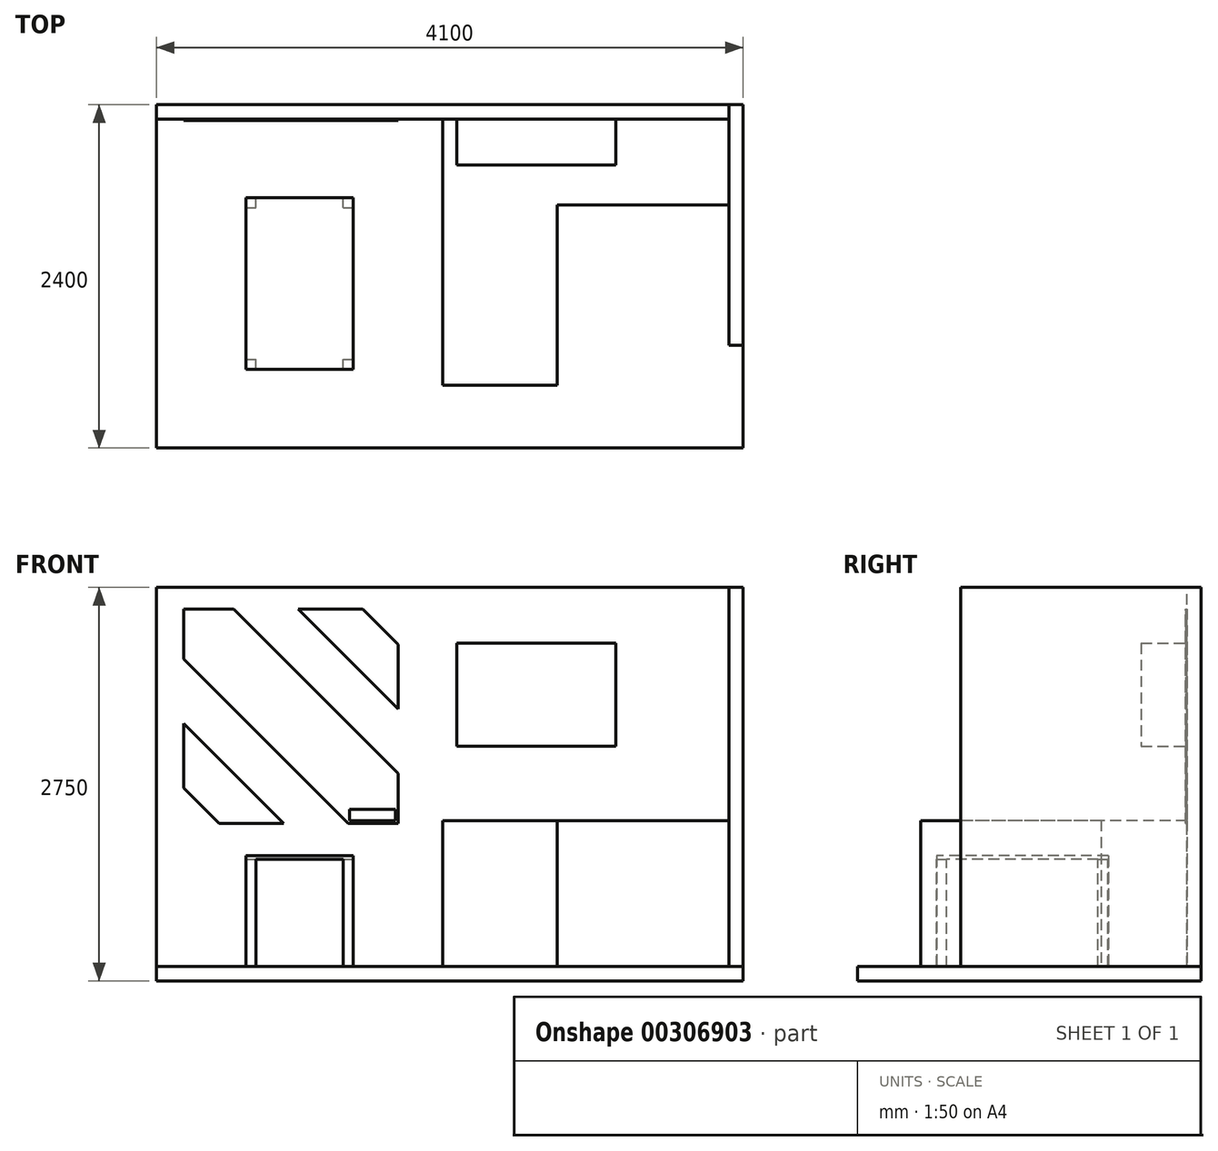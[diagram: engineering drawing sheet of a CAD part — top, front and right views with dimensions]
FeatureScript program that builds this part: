
annotation { "Feature Type Name" : "Feature", "Feature Type Description" : "" }
export const myFeature = defineFeature(function(context is Context, id is Id, definition is map)
    precondition{}
    {
        {
            var Q0;
            Q0=qCreatedBy(makeId("Top.planeOp"),FACE);
            var sketch = newSketch(context, id + "F0", { "sketchPlane" : qUnion([Q0])});
            skLineSegment(sketch, "E0.bottom", {"start": v(0, 0) * mm, "end": v(800, 0) * mm});
            skLineSegment(sketch, "E0.top", {"start": v(0, -1860) * mm, "end": v(800, -1860) * mm});
            skLineSegment(sketch, "E0.left", {"start": v(0, 0) * mm, "end": v(0, -1860) * mm});
            skLineSegment(sketch, "E0.right", {"start": v(800, -600) * mm, "end": v(800, -1860) * mm});
            skLineSegment(sketch, "E1", {"start": v(800, 0) * mm, "end": v(2000, 0) * mm});
            skLineSegment(sketch, "E2", {"start": v(2000, 0) * mm, "end": v(2000, -600) * mm});
            skLineSegment(sketch, "E3", {"start": v(2000, -600) * mm, "end": v(800, -600) * mm});
            skSolve(sketch);
        }
        {
            var Q0;
            Q0=makeQuery(id+"F0.imprint","IMPRINT",FACE,{"disambiguationData":[TD([[makeQuery(id+"F0.imprint","IMPRINT",EDGE,{"derivedFrom":sQuery(id+"F0.wireOp",EDGE,"E0.bottom")}),-1.0]])]});
            extrude(context, id + "F1", {"entities" : qUnion([Q0]), "depth" : 1020 * mm});
        }
        {
            var Q0;
            Q0=makeQuery(id+"F1.opExtrude","SWEPT_FACE",FACE,{"disambiguationData":[OSD([sQuery(id+"F0.wireOp",EDGE,"E0.bottom"),sQuery(id+"F0.wireOp",EDGE,"E1")])]});
            cPlane(context, id + "F2", {"entities" : qUnion([Q0]), "cplaneType" : CPlaneType.OFFSET, "offset" : 0 * mm, "width" : 150 * mm, "height" : 150 * mm});
        }
        {
            var Q0;
            Q0=qCreatedBy(id+"F2.planeOp",FACE);
            var sketch = newSketch(context, id + "F3", { "sketchPlane" : qUnion([Q0])});
            skLineSegment(sketch, "E4.0", {"start": v(0, 1020) * mm, "end": v(0, 0) * mm, "construction": true});
            skLineSegment(sketch, "E5.bottom", {"start": v(0, 0) * mm, "end": v(2000, 0) * mm});
            skLineSegment(sketch, "E5.top", {"start": v(0, 2650) * mm, "end": v(2000, 2650) * mm});
            skLineSegment(sketch, "E5.left", {"start": v(0, 0) * mm, "end": v(0, 2650) * mm, "construction": true});
            skLineSegment(sketch, "E5.right", {"start": v(2000, 0) * mm, "end": v(2000, 2650) * mm});
            skLineSegment(sketch, "E6.0", {"start": v(-2000, 1020) * mm, "end": v(-2000, 0) * mm, "construction": true});
            skLineSegment(sketch, "E7.bottom", {"start": v(0, 0) * mm, "end": v(-2000, 0) * mm});
            skLineSegment(sketch, "E7.top", {"start": v(0, 2650) * mm, "end": v(-2000, 2650) * mm});
            skLineSegment(sketch, "E7.right", {"start": v(-2000, 0) * mm, "end": v(-2000, 2650) * mm});
            skLineSegment(sketch, "E8.bottom", {"start": v(-1210, 2260) * mm, "end": v(-100, 2260) * mm});
            skLineSegment(sketch, "E8.top", {"start": v(-1210, 1540) * mm, "end": v(-100, 1540) * mm});
            skLineSegment(sketch, "E8.left", {"start": v(-1210, 2260) * mm, "end": v(-1210, 1540) * mm});
            skLineSegment(sketch, "E8.right", {"start": v(-100, 2260) * mm, "end": v(-100, 1540) * mm});
            skSolve(sketch);
        }
        {
            var Q0;
            Q0=makeQuery(id+"F3.imprint","IMPRINT",FACE,{"disambiguationData":[TD([[makeQuery(id+"F3.imprint","IMPRINT",EDGE,{"derivedFrom":sQuery(id+"F3.wireOp",EDGE,"E5.bottom")}),1.0]])]});
            var Q1;
            Q1=makeQuery(id+"F3.imprint","IMPRINT",FACE,{"disambiguationData":[TD([[makeQuery(id+"F3.imprint","IMPRINT",EDGE,{"derivedFrom":sQuery(id+"F3.wireOp",EDGE,"E8.bottom")}),-1.0]])]});
            extrude(context, id + "F4", {"entities" : qUnion([Q0, Q1]), "depth" : 100 * mm});
        }
        {
            var Q0;
            Q0=makeQuery(id+"F3.imprint","IMPRINT",FACE,{"disambiguationData":[TD([[makeQuery(id+"F3.imprint","IMPRINT",EDGE,{"derivedFrom":sQuery(id+"F3.wireOp",EDGE,"E8.bottom")}),-1.0]])]});
            extrude(context, id + "F5", {"entities" : qUnion([Q0]), "oppositeDirection" : true, "depth" : 320 * mm});
        }
        {
            var Q0;
            Q0=makeQuery(id+"F1.opExtrude","SWEPT_FACE",FACE,{"disambiguationData":[OSD([sQuery(id+"F0.wireOp",EDGE,"E2")])]});
            cPlane(context, id + "F6", {"entities" : qUnion([Q0]), "cplaneType" : CPlaneType.OFFSET, "offset" : 0 * mm, "width" : 150 * mm, "height" : 150 * mm});
        }
        {
            var Q0;
            Q0=qCreatedBy(id+"F6.planeOp",FACE);
            var sketch = newSketch(context, id + "F7", { "sketchPlane" : qUnion([Q0])});
            skPoint(sketch, "E9.0", {"position": v(100, 0) * mm});
            skPoint(sketch, "E10.0", {"position": v(100, 2650) * mm});
            skLineSegment(sketch, "E11.bottom", {"start": v(100, 0) * mm, "end": v(-1580, 0) * mm});
            skLineSegment(sketch, "E11.top", {"start": v(100, 2650) * mm, "end": v(-1580, 2650) * mm});
            skLineSegment(sketch, "E11.left", {"start": v(100, 0) * mm, "end": v(100, 2650) * mm});
            skLineSegment(sketch, "E11.right", {"start": v(-1580, 0) * mm, "end": v(-1580, 2650) * mm});
            skSolve(sketch);
        }
        {
            var Q0;
            Q0=makeQuery(id+"F7.imprint","IMPRINT",FACE,{"disambiguationData":[TD([[makeQuery(id+"F7.imprint","IMPRINT",EDGE,{"derivedFrom":sQuery(id+"F7.wireOp",EDGE,"E11.bottom")}),-1.0]])]});
            extrude(context, id + "F8", {"entities" : qUnion([Q0]), "depth" : 100 * mm});
        }
        {
            var Q0;
            Q0=makeQuery(id+"F1.opExtrude","CAP_FACE",FACE,{"disambiguationData":[OSD([sQuery(id+"F0.wireOp",EDGE,"E0.bottom"),sQuery(id+"F0.wireOp",EDGE,"E0.top"),sQuery(id+"F0.wireOp",EDGE,"E0.left"),sQuery(id+"F0.wireOp",EDGE,"E0.right"),sQuery(id+"F0.wireOp",EDGE,"E1"),sQuery(id+"F0.wireOp",EDGE,"E2"),sQuery(id+"F0.wireOp",EDGE,"E3")])],"isStart":true});
            cPlane(context, id + "F9", {"entities" : qUnion([Q0]), "cplaneType" : CPlaneType.OFFSET, "offset" : 0 * mm, "width" : 150 * mm, "height" : 150 * mm});
        }
        {
            var Q0;
            Q0=qCreatedBy(id+"F9.planeOp",FACE);
            var sketch = newSketch(context, id + "F10", { "sketchPlane" : qUnion([Q0])});
            skPoint(sketch, "E12.0", {"position": v(2100, -100) * mm});
            skPoint(sketch, "E13.0", {"position": v(-2000, -100) * mm});
            skLineSegment(sketch, "E14.bottom", {"start": v(2100, -100) * mm, "end": v(-2000, -100) * mm});
            skLineSegment(sketch, "E14.top", {"start": v(2100, 2300) * mm, "end": v(-2000, 2300) * mm});
            skLineSegment(sketch, "E14.left", {"start": v(2100, -100) * mm, "end": v(2100, 2300) * mm});
            skLineSegment(sketch, "E14.right", {"start": v(-2000, -100) * mm, "end": v(-2000, 2300) * mm});
            skSolve(sketch);
        }
        {
            var Q0;
            Q0=makeQuery(id+"F10.imprint","IMPRINT",FACE,{"disambiguationData":[TD([[makeQuery(id+"F10.imprint","IMPRINT",EDGE,{"derivedFrom":sQuery(id+"F10.wireOp",EDGE,"E14.bottom")}),-1.0]])]});
            extrude(context, id + "F11", {"entities" : qUnion([Q0]), "depth" : 100 * mm});
        }
        {
            var Q0;
            Q0=makeQuery(id+"F11.opExtrude","CAP_FACE",FACE,{"disambiguationData":[OSD([sQuery(id+"F10.wireOp",EDGE,"E14.bottom"),sQuery(id+"F10.wireOp",EDGE,"E14.top"),sQuery(id+"F10.wireOp",EDGE,"E14.left"),sQuery(id+"F10.wireOp",EDGE,"E14.right")])],"isStart":true});
            var sketch = newSketch(context, id + "F12", { "sketchPlane" : qUnion([Q0])});
            skLineSegment(sketch, "E15.bottom", {"start": v(-1375, -550) * mm, "end": v(-625, -550) * mm});
            skLineSegment(sketch, "E15.top", {"start": v(-1375, -1750) * mm, "end": v(-625, -1750) * mm});
            skLineSegment(sketch, "E15.left", {"start": v(-1375, -550) * mm, "end": v(-1375, -1750) * mm});
            skLineSegment(sketch, "E15.right", {"start": v(-625, -550) * mm, "end": v(-625, -1750) * mm});
            skLineSegment(sketch, "E16", {"start": v(-1375, -1150) * mm, "end": v(-2000, -1150) * mm, "construction": true});
            skLineSegment(sketch, "E17", {"start": v(-625, -1150) * mm, "end": v(0, -1150) * mm, "construction": true});
            skLineSegment(sketch, "E18", {"start": v(-1000, -550) * mm, "end": v(-1000, 0) * mm, "construction": true});
            skLineSegment(sketch, "E19", {"start": v(-1000, -1750) * mm, "end": v(-1000, -2300) * mm, "construction": true});
            skSolve(sketch);
        }
        {
            var Q0;
            Q0=makeQuery(id+"F12.imprint","IMPRINT",FACE,{"disambiguationData":[TD([[makeQuery(id+"F12.imprint","IMPRINT",EDGE,{"derivedFrom":sQuery(id+"F12.wireOp",EDGE,"E15.bottom")}),-1.0]])]});
            extrude(context, id + "F13", {"entities" : qUnion([Q0]), "depth" : 25 * mm});
        }
        {
            var Q0;
            Q0=makeQuery(id+"F13.opExtrude","SWEPT_BODY",BODY,{"disambiguationData":[OSD([sQuery(id+"F12.wireOp",EDGE,"E15.bottom"),sQuery(id+"F12.wireOp",EDGE,"E15.top"),sQuery(id+"F12.wireOp",EDGE,"E15.left"),sQuery(id+"F12.wireOp",EDGE,"E15.right")])]});
            var Q1;
            Q1=makeQuery(id+"F13.opExtrude","CAP_FACE",FACE,{"disambiguationData":[OSD([sQuery(id+"F12.wireOp",EDGE,"E15.bottom"),sQuery(id+"F12.wireOp",EDGE,"E15.top"),sQuery(id+"F12.wireOp",EDGE,"E15.left"),sQuery(id+"F12.wireOp",EDGE,"E15.right")])],"isStart":false});
            transform(context, id + "F14", {"entities" : qUnion([Q0]), "transformType" : TransformType.TRANSLATION_DISTANCE, "transformDirection" : qUnion([Q1]), "distance" : 750 * mm, "makeCopy" : false});
        }
        {
            var Q0;
            Q0=makeQuery(id+"F13.opExtrude","CAP_FACE",FACE,{"disambiguationData":[OSD([sQuery(id+"F12.wireOp",EDGE,"E15.bottom"),sQuery(id+"F12.wireOp",EDGE,"E15.top"),sQuery(id+"F12.wireOp",EDGE,"E15.left"),sQuery(id+"F12.wireOp",EDGE,"E15.right")])],"isStart":true});
            var sketch = newSketch(context, id + "F15", { "sketchPlane" : qUnion([Q0])});
            skLineSegment(sketch, "E20.bottom", {"start": v(-1375, 1750) * mm, "end": v(-1305, 1750) * mm});
            skLineSegment(sketch, "E20.top", {"start": v(-1375, 1680) * mm, "end": v(-1305, 1680) * mm});
            skLineSegment(sketch, "E20.left", {"start": v(-1375, 1750) * mm, "end": v(-1375, 1680) * mm});
            skLineSegment(sketch, "E20.right", {"start": v(-1305, 1750) * mm, "end": v(-1305, 1680) * mm});
            skLineSegment(sketch, "E21.0.1.0", {"start": v(-1305, 620) * mm, "end": v(-1305, 550) * mm});
            skLineSegment(sketch, "E21.0.1.1", {"start": v(-1375, 620) * mm, "end": v(-1305, 620) * mm});
            skLineSegment(sketch, "E21.0.1.2", {"start": v(-1375, 620) * mm, "end": v(-1375, 550) * mm});
            skLineSegment(sketch, "E21.0.1.3", {"start": v(-1375, 550) * mm, "end": v(-1305, 550) * mm});
            skLineSegment(sketch, "E21.1.0.0", {"start": v(-625, 1750.1) * mm, "end": v(-625, 1680.1) * mm});
            skLineSegment(sketch, "E21.1.0.1", {"start": v(-695, 1750.1) * mm, "end": v(-625, 1750.1) * mm});
            skLineSegment(sketch, "E21.1.0.2", {"start": v(-695, 1750.1) * mm, "end": v(-695, 1680.1) * mm});
            skLineSegment(sketch, "E21.1.0.3", {"start": v(-695, 1680.1) * mm, "end": v(-625, 1680.1) * mm});
            skLineSegment(sketch, "E21.1.1.0", {"start": v(-625, 620.1) * mm, "end": v(-625, 550.1) * mm});
            skLineSegment(sketch, "E21.1.1.1", {"start": v(-695, 620.1) * mm, "end": v(-625, 620.1) * mm});
            skLineSegment(sketch, "E21.1.1.2", {"start": v(-695, 620.1) * mm, "end": v(-695, 550.1) * mm});
            skLineSegment(sketch, "E21.1.1.3", {"start": v(-695, 550.1) * mm, "end": v(-625, 550.1) * mm});
            skLineSegment(sketch, "E21.direction1", {"start": v(-1305, 1680) * mm, "end": v(-625, 1680.1) * mm, "construction": true});
            skLineSegment(sketch, "E21.direction2", {"start": v(-1305, 1680) * mm, "end": v(-1305, 550) * mm, "construction": true});
            skSolve(sketch);
        }
        {
            var Q0;
            Q0=makeQuery(id+"F15.imprint","IMPRINT",FACE,{"disambiguationData":[TD([[makeQuery(id+"F15.imprint","IMPRINT",EDGE,{"derivedFrom":sQuery(id+"F15.wireOp",EDGE,"E20.bottom")}),-1.0]])]});
            var Q1;
            {var subQ3=sQuery(id+"F15.wireOp",EDGE,"E21.1.0.3");Q1=makeQuery(id+"F15.imprint","IMPRINT",FACE,{"disambiguationData":[TD([[makeQuery(id+"F15.imprint","IMPRINT",EDGE,{"derivedFrom":subQ3}),1.0]])]});}
            var Q2;
            Q2=makeQuery(id+"F15.imprint","IMPRINT",FACE,{"disambiguationData":[TD([[makeQuery(id+"F15.imprint","IMPRINT",EDGE,{"derivedFrom":sQuery(id+"F15.wireOp",EDGE,"E21.1.1.0")}),1.0]])]});
            var Q3;
            Q3=makeQuery(id+"F15.imprint","IMPRINT",FACE,{"disambiguationData":[TD([[makeQuery(id+"F15.imprint","IMPRINT",EDGE,{"derivedFrom":sQuery(id+"F15.wireOp",EDGE,"E21.0.1.0")}),-1.0]])]});
            extrude(context, id + "F16", {"entities" : qUnion([Q0, Q1, Q2, Q3]), "operationType" : NewBodyOperationType.ADD, "depth" : 750 * mm});
        }
        {
            var Q0;
            Q0=makeQuery(id+"F4.opExtrude","CAP_FACE",FACE,{"disambiguationData":[OSD([sQuery(id+"F3.wireOp",EDGE,"E5.bottom"),sQuery(id+"F3.wireOp",EDGE,"E5.top"),sQuery(id+"F3.wireOp",EDGE,"E5.right"),sQuery(id+"F3.wireOp",EDGE,"E7.bottom"),sQuery(id+"F3.wireOp",EDGE,"E7.top"),sQuery(id+"F3.wireOp",EDGE,"E7.right")])],"isStart":true});
            cPlane(context, id + "F17", {"entities" : qUnion([Q0]), "cplaneType" : CPlaneType.OFFSET, "offset" : 0 * mm, "width" : 150 * mm, "height" : 150 * mm});
        }
        {
            var Q0;
            Q0=qCreatedBy(id+"F17.planeOp",FACE);
            var sketch = newSketch(context, id + "F18", { "sketchPlane" : qUnion([Q0])});
            skLineSegment(sketch, "E22.0", {"start": v(-2000, 0) * mm, "end": v(-2000, 2650) * mm, "construction": true});
            skLineSegment(sketch, "E23.0", {"start": v(2100, 0) * mm, "end": v(-2000, 0) * mm, "construction": true});
            skLineSegment(sketch, "E24.bottom", {"start": v(-650, 1100) * mm, "end": v(-330, 1100) * mm});
            skLineSegment(sketch, "E24.top", {"start": v(-650, 1020) * mm, "end": v(-330, 1020) * mm});
            skLineSegment(sketch, "E24.left", {"start": v(-650, 1100) * mm, "end": v(-650, 1020) * mm});
            skLineSegment(sketch, "E24.right", {"start": v(-330, 1100) * mm, "end": v(-330, 1020) * mm});
            skSolve(sketch);
        }
        {
            var Q0;
            Q0=makeQuery(id+"F18.imprint","IMPRINT",FACE,{"disambiguationData":[TD([[makeQuery(id+"F18.imprint","IMPRINT",EDGE,{"derivedFrom":sQuery(id+"F18.wireOp",EDGE,"E24.bottom")}),-1.0]])]});
            extrude(context, id + "F19", {"entities" : qUnion([Q0]), "depth" : 10 * mm});
        }
        {
            var Q0;
            Q0=qCreatedBy(id+"F17.planeOp",FACE);
            var sketch = newSketch(context, id + "F20", { "sketchPlane" : qUnion([Q0])});
            skPoint(sketch, "E25.0", {"position": v(-330, 1020) * mm});
            skLineSegment(sketch, "E26", {"start": v(-660, 1000) * mm, "end": v(-1810, 2150) * mm});
            skLineSegment(sketch, "E27", {"start": v(-1810, 2500) * mm, "end": v(-310, 1000) * mm, "construction": true});
            skLineSegment(sketch, "E28.MirrorCS", {"start": v(-310, 1350) * mm, "end": v(-1460, 2500) * mm});
            skLineSegment(sketch, "E29", {"start": v(-1810, 2500) * mm, "end": v(-1460, 2500) * mm});
            skLineSegment(sketch, "E30", {"start": v(-310, 1350) * mm, "end": v(-310, 1000) * mm});
            skLineSegment(sketch, "E31", {"start": v(-660, 1000) * mm, "end": v(-310, 1000) * mm});
            skLineSegment(sketch, "E32", {"start": v(-1810, 2500) * mm, "end": v(-1810, 2150) * mm});
            skLineSegment(sketch, "E33", {"start": v(-1460, 2500) * mm, "end": v(-310, 2500) * mm, "construction": true});
            skLineSegment(sketch, "E34", {"start": v(-310, 2500) * mm, "end": v(-310, 1350) * mm, "construction": true});
            skLineSegment(sketch, "E35", {"start": v(-660, 1000) * mm, "end": v(-1810, 1000) * mm, "construction": true});
            skLineSegment(sketch, "E36", {"start": v(-1810, 1000) * mm, "end": v(-1810, 2150) * mm, "construction": true});
            skLineSegment(sketch, "E37", {"start": v(-557.49, 2500) * mm, "end": v(-310, 2252.51) * mm});
            skLineSegment(sketch, "E38", {"start": v(-310, 1801.01) * mm, "end": v(-1008.99, 2500) * mm});
            skLineSegment(sketch, "E39", {"start": v(-1008.99, 2500) * mm, "end": v(-557.49, 2500) * mm});
            skLineSegment(sketch, "E40", {"start": v(-310, 2252.51) * mm, "end": v(-310, 1801.01) * mm});
            skLineSegment(sketch, "E41.MirrorCS", {"start": v(-1111.01, 1000) * mm, "end": v(-1810, 1698.99) * mm});
            skLineSegment(sketch, "E42.MirrorCS", {"start": v(-1810, 1247.49) * mm, "end": v(-1562.51, 1000) * mm});
            skLineSegment(sketch, "E43.MirrorCS", {"start": v(-1562.51, 1000) * mm, "end": v(-1111.01, 1000) * mm});
            skLineSegment(sketch, "E44.MirrorCS", {"start": v(-1810, 1698.99) * mm, "end": v(-1810, 1247.49) * mm});
            skSolve(sketch);
        }
        {
            var Q0;
            Q0=makeQuery(id+"F20.imprint","IMPRINT",FACE,{"disambiguationData":[TD([[makeQuery(id+"F20.imprint","IMPRINT",EDGE,{"derivedFrom":sQuery(id+"F20.wireOp",EDGE,"E26")}),-1.0]])]});
            var Q1;
            Q1=makeQuery(id+"F20.imprint","IMPRINT",FACE,{"disambiguationData":[TD([[makeQuery(id+"F20.imprint","IMPRINT",EDGE,{"derivedFrom":sQuery(id+"F20.wireOp",EDGE,"E37")}),-1.0]])]});
            var Q2;
            Q2=makeQuery(id+"F20.imprint","IMPRINT",FACE,{"disambiguationData":[TD([[makeQuery(id+"F20.imprint","IMPRINT",EDGE,{"derivedFrom":sQuery(id+"F20.wireOp",EDGE,"E41.MirrorCS")}),1.0]])]});
            extrude(context, id + "F21", {"entities" : qUnion([Q0, Q1, Q2]), "depth" : 10 * mm});
        }
    });
